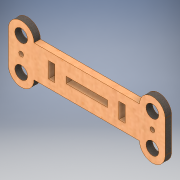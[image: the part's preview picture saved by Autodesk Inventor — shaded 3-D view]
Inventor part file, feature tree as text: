
AUTODESK INVENTOR PART (.ipt)
format: ipt  version: 2019 (Build 230136000, 136)  size: 181,760 bytes
history: native  units: mm
features: sketch x2, other x1, extrude x1, hole x1, projected_geometry x1
ambient origin geometry x8: Origin, YZ Plane, XZ Plane, XY Plane, X Axis, Y Axis, Z Axis, Center Point
bodies: Body1 (feature_tree)
feature tree (6):
  other  "Твердое тело1"
  extrude  "Выдавливание1"  Depth=8.0mm
  hole  "Отверстие1"  [1 undecoded]
  sketch  "Эскиз1"
  sketch  "Эскиз2"
  projected_geometry  "Спроецированная петля1"
note: 1 required parameter value undecoded (feature->parameter linkage not recoverable at this tier; creation-order binding heuristic only, values carry confidence <= 0.55)
